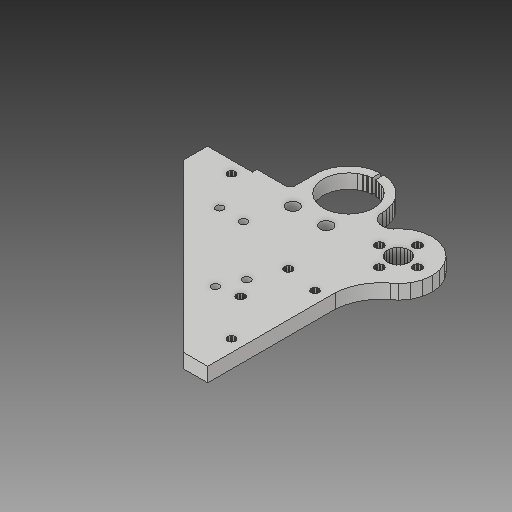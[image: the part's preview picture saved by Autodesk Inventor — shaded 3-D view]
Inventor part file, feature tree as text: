
AUTODESK INVENTOR PART (.ipt)
format: ipt  version: 2018 (Build 220112000, 112)  size: 601,600 bytes
history: native  units: mm
features: other x3, sketch x2
ambient origin geometry x8: Origin, YZ Plane, XZ Plane, XY Plane, X Axis, Y Axis, Z Axis, Center Point
bodies: Solid1 (feature_tree)
feature tree (5):
  other  "Left Bed Holder Lower.ipt"
  other  "Solid1::Left Bed Holder Lower.ipt"
  other  "TaggingFeature1"
  sketch  "Sketch2"  dims[d0=10.0mm]
  sketch  "Sketch4"
